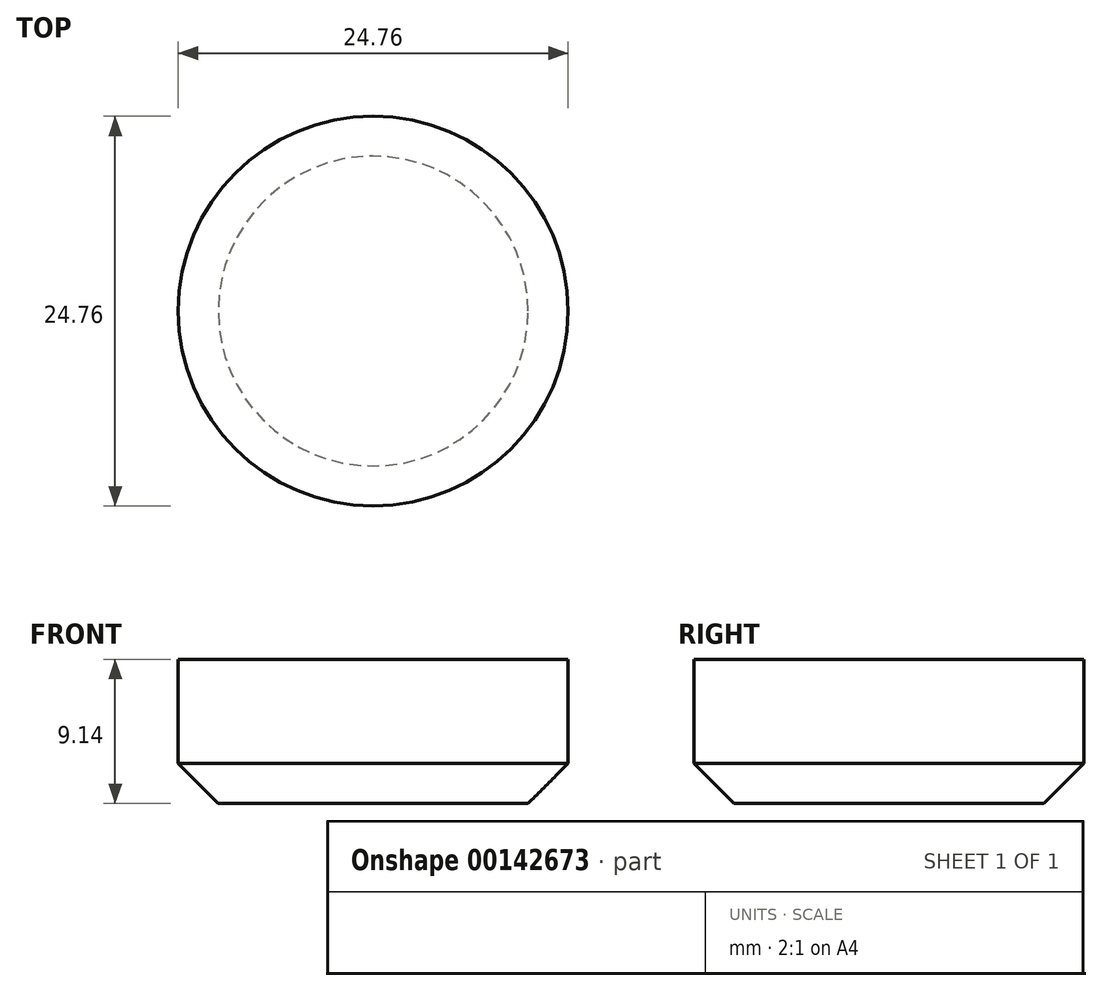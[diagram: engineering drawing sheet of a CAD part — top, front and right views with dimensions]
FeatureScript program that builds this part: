
annotation { "Feature Type Name" : "Feature", "Feature Type Description" : "" }
export const myFeature = defineFeature(function(context is Context, id is Id, definition is map)
    precondition{}
    {
        {
            var Q0;
            Q0=qCreatedBy(makeId("Top.planeOp"),FACE);
            var sketch = newSketch(context, id + "F0", { "sketchPlane" : qUnion([Q0])});
            skCircle(sketch, "E0", {"center": v(0, 0) * mm, "radius": 12.38 * mm});
            skSolve(sketch);
        }
        {
            var Q0;
            Q0=makeQuery(id+"F0.imprint","IMPRINT",FACE,{"disambiguationData":[TD([[makeQuery(id+"F0.imprint","IMPRINT",EDGE,{"derivedFrom":sQuery(id+"F0.wireOp",EDGE,"E0")}),1.0]])]});
            extrude(context, id + "F1", {"entities" : qUnion([Q0]), "depth" : 9.14 * mm});
        }
        {
            var Q0;
            Q0=makeQuery(id+"F1.opExtrude","CAP_EDGE",EDGE,{"disambiguationData":[OSD([sQuery(id+"F0.wireOp",EDGE,"E0")])],"isStart":true});
            chamfer(context, id + "F2", {"entities" : qUnion([Q0]), "width" : 2.54 * mm, "tangentPropagation" : true});
        }
    });
